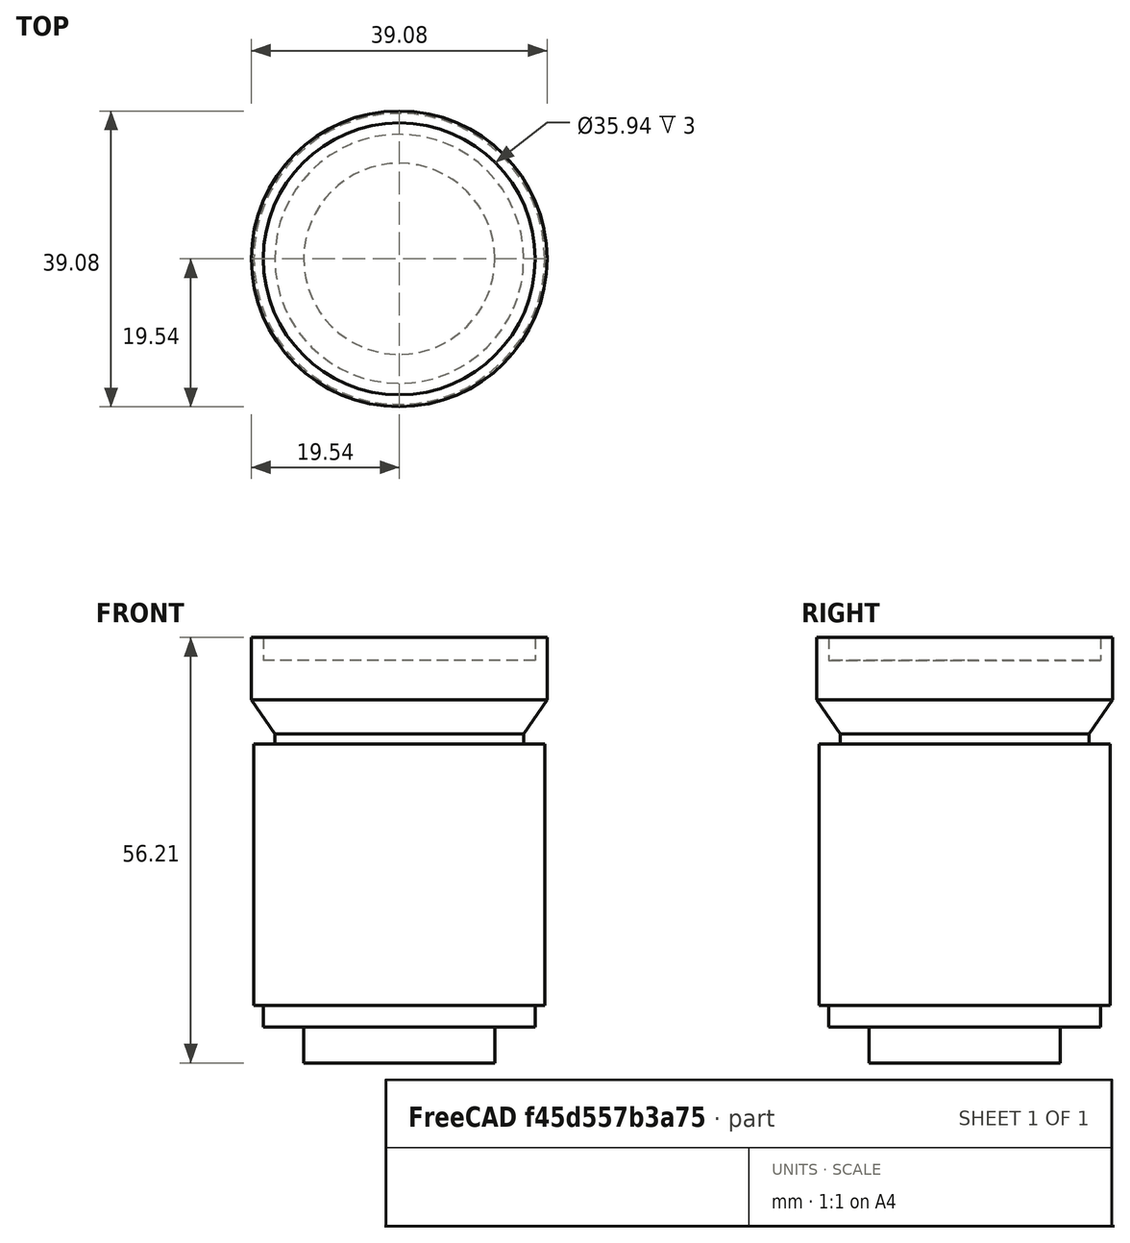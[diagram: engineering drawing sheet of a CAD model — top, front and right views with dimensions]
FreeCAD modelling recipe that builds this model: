
FCSTD DOCUMENT  (FreeCAD 0.18.4R)
Label: telephotolens
License: All rights reserved
LicenseURL: http://en.wikipedia.org/wiki/All_rights_reserved
objects: Sketcher::SketchObject×1, PartDesign::Revolution×1, PartDesign::Body×1
note: 4 computed .brp shape members not serialized (recipe doc carries the construction recipe); baked Part::Feature solids carry a one-line shape summary decoded from their .brp

FEATURE [Sketcher::SketchObject] Sketch
  MapMode = 5
  Placement = pos=(0,0,0) rot=(1,0,0;1.5708rad)
  Support = -> [XZ_Plane]
  sketch-geometry (14):
    g0: LineSegment StartX=0 StartY=0 StartZ=0 EndX=12.63 EndY=0 EndZ=0
    g1: LineSegment StartX=12.63 StartY=0 StartZ=0 EndX=12.63 EndY=4.75 EndZ=0
    g2: LineSegment StartX=12.63 StartY=4.75 StartZ=0 EndX=17.975 EndY=4.75 EndZ=0
    g3: LineSegment StartX=17.975 StartY=4.75 StartZ=0 EndX=17.975 EndY=7.6 EndZ=0
    g4: LineSegment StartX=17.975 StartY=7.6 StartZ=0 EndX=19.225 EndY=7.6 EndZ=0
    g5: LineSegment StartX=19.225 StartY=7.6 StartZ=0 EndX=19.225 EndY=42.11 EndZ=0
    g6: LineSegment StartX=19.225 StartY=42.11 StartZ=0 EndX=16.455 EndY=42.11 EndZ=0
    g7: LineSegment StartX=16.455 StartY=42.11 StartZ=0 EndX=16.455 EndY=43.48 EndZ=0
    g8: LineSegment StartX=16.455 StartY=43.48 StartZ=0 EndX=19.54 EndY=47.99 EndZ=0
    g9: LineSegment StartX=19.54 StartY=47.99 StartZ=0 EndX=19.54 EndY=56.21 EndZ=0
    g10: LineSegment StartX=0 StartY=53.21 StartZ=0 EndX=0 EndY=0 EndZ=0
    g11: LineSegment StartX=19.54 StartY=56.21 StartZ=0 EndX=17.97 EndY=56.21 EndZ=0
    g12: LineSegment StartX=17.97 StartY=56.21 StartZ=0 EndX=17.97 EndY=53.21 EndZ=0
    g13: LineSegment StartX=17.97 StartY=53.21 StartZ=0 EndX=0 EndY=53.21 EndZ=0
  constraints (41):
    c: PointOnObject(g0,g-1)
    c: Coincident(g-1,g0)
    c: Distance(g0) = 12.63
    c: Vertical(g1)
    c: Distance(g1) = 4.75
    c: Coincident(g1,g0)
    c: Horizontal(g2)
    c: DistanceX(g-2,g2) = 17.975
    c: Coincident(g2,g1)
    c: Coincident(g2,g3)
    c: Vertical(g3)
    c: Distance(g3) = 2.85
    c: Coincident(g4,g5)
    c: Coincident(g5,g6)
    c: Coincident(g6,g7)
    c: Coincident(g7,g8)
    c: Coincident(g8,g9)
    c: Horizontal(g4)
    c: Vertical(g5)
    c: Horizontal(g6)
    c: Vertical(g7)
    c: Vertical(g9)
    c: Coincident(g4,g3)
    c: Distance(g4) = 1.25
    c: Distance(g5) = 34.51
    c: Distance(g6) = 2.77
    c: Distance(g7) = 1.37
    c: Distance(g9) = 8.22
    c: Coincident(g0,g10)
    c: PointOnObject(g10,g-2)
    c: Distance(g9,g2) = 51.46
    c: Coincident(g11,g12)
    c: Coincident(g12,g13)
    c: Horizontal(g13)
    c: Vertical(g12)
    c: Distance(g12) = 3
    c: Coincident(g13,g10)
    c: Horizontal(g11)
    c: Distance(g11) = 1.57
    c: Coincident(g9,g11)
    c: DistanceX(g-2,g9) = 19.54
FEATURE [PartDesign::Revolution] Revolution
  Angle = 360
  Axis = (0,2e-16,1)
  Base = (0,0,0)
  Placement = pos=(0,0,0) rot=(1,0,0;1.5708rad)
  Profile = -> Sketch
  ReferenceAxis = -> Sketch [V_Axis]
  Reversed = true
FEATURE [PartDesign::Body] Body
  Group = -> [Sketch,Revolution]
  Origin = -> Origin
  Tip = -> Revolution
